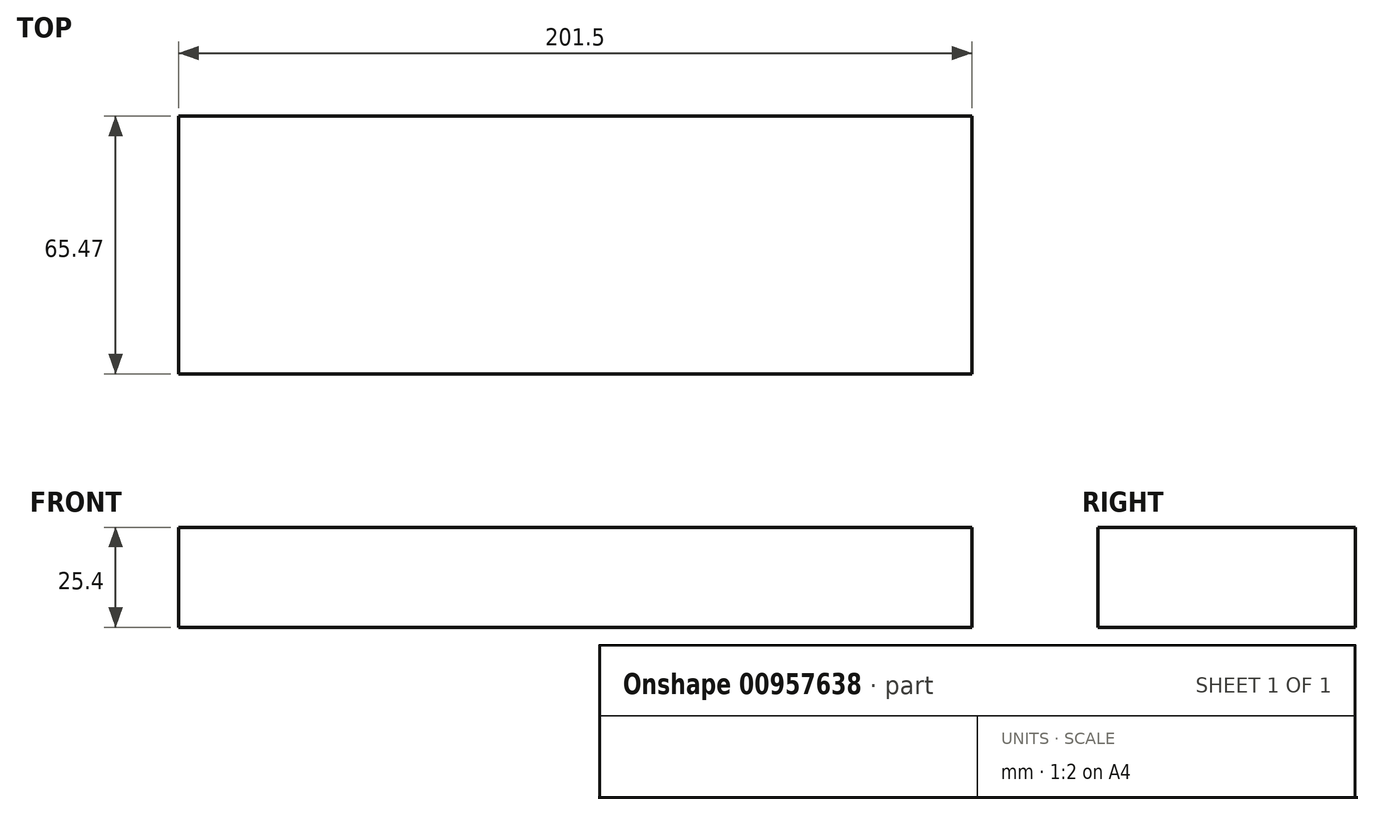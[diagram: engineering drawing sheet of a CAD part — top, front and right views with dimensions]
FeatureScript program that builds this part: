
annotation { "Feature Type Name" : "Feature", "Feature Type Description" : "" }
export const myFeature = defineFeature(function(context is Context, id is Id, definition is map)
    precondition{}
    {
        {
            var Q0;
            Q0=qCreatedBy(makeId("Top.planeOp"),FACE);
            var sketch = newSketch(context, id + "F0", { "sketchPlane" : qUnion([Q0])});
            skLineSegment(sketch, "E0.bottom", {"start": v(-127.9, -15.22) * mm, "end": v(73.6, -15.22) * mm});
            skLineSegment(sketch, "E0.top", {"start": v(-127.9, -80.7) * mm, "end": v(73.6, -80.7) * mm});
            skLineSegment(sketch, "E0.left", {"start": v(-127.9, -15.22) * mm, "end": v(-127.9, -80.7) * mm});
            skLineSegment(sketch, "E0.right", {"start": v(73.6, -15.22) * mm, "end": v(73.6, -80.7) * mm});
            skSolve(sketch);
        }
        {
            var Q0;
            Q0=makeQuery(id+"F0.imprint","IMPRINT",FACE,{"disambiguationData":[TD([[makeQuery(id+"F0.imprint","IMPRINT",EDGE,{"derivedFrom":sQuery(id+"F0.wireOp",EDGE,"E0.bottom")}),-1.0]])]});
            extrude(context, id + "F1", {"entities" : qUnion([Q0]), "depth" : 25.4 * mm, "offsetDistance" : 25.4 * mm});
        }
    });
